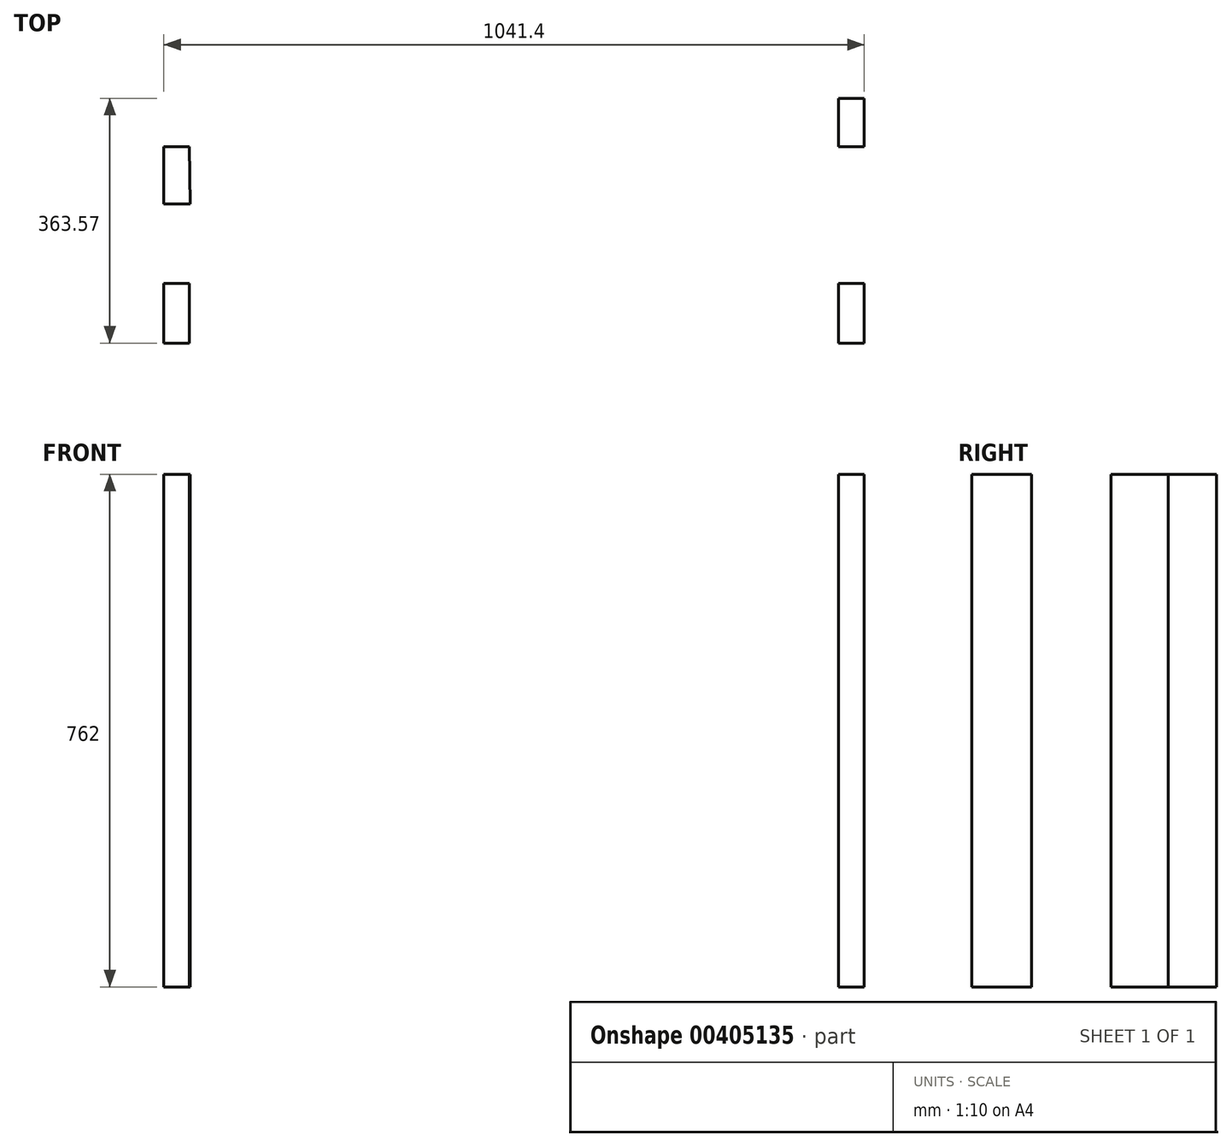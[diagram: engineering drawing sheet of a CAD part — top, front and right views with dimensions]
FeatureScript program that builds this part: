
annotation { "Feature Type Name" : "Feature", "Feature Type Description" : "" }
export const myFeature = defineFeature(function(context is Context, id is Id, definition is map)
    precondition{}
    {
        {
            var Q0;
            Q0=qCreatedBy(makeId("Top.planeOp"),FACE);
            var sketch = newSketch(context, id + "F0", { "sketchPlane" : qUnion([Q0])});
            skLineSegment(sketch, "E0.bottom", {"start": v(0, 0) * mm, "end": v(38.1, 0) * mm});
            skLineSegment(sketch, "E0.top", {"start": v(0, 0) * mm, "end": v(38.1, 0) * mm});
            skLineSegment(sketch, "E0.left", {"start": v(0, 0) * mm, "end": v(0, 0) * mm});
            skLineSegment(sketch, "E0.right", {"start": v(38.1, 0) * mm, "end": v(38.1, 0) * mm});
            skLineSegment(sketch, "E1.bottom", {"start": v(0, -292.1) * mm, "end": v(38.1, -292.1) * mm});
            skLineSegment(sketch, "E1.top", {"start": v(0, -203.2) * mm, "end": v(38.1, -203.2) * mm});
            skLineSegment(sketch, "E1.left", {"start": v(0, -292.1) * mm, "end": v(0, -203.2) * mm});
            skLineSegment(sketch, "E1.right", {"start": v(38.1, -292.1) * mm, "end": v(38.1, -203.2) * mm});
            skLineSegment(sketch, "E2.bottom", {"start": v(1041.4, 0) * mm, "end": v(1003.3, 0) * mm});
            skLineSegment(sketch, "E2.top", {"start": v(1041.4, 0) * mm, "end": v(1003.3, 0) * mm});
            skLineSegment(sketch, "E2.left", {"start": v(1003.3, 0) * mm, "end": v(1003.3, 0) * mm});
            skLineSegment(sketch, "E2.right", {"start": v(1041.4, 0) * mm, "end": v(1041.4, 0) * mm});
            skLineSegment(sketch, "E3.bottom", {"start": v(1003.3, -203.2) * mm, "end": v(1041.4, -203.2) * mm});
            skLineSegment(sketch, "E3.top", {"start": v(1003.3, -292.1) * mm, "end": v(1041.4, -292.1) * mm});
            skLineSegment(sketch, "E3.left", {"start": v(1003.3, -203.2) * mm, "end": v(1003.3, -292.1) * mm});
            skLineSegment(sketch, "E3.right", {"start": v(1041.4, -203.2) * mm, "end": v(1041.4, -292.1) * mm});
            skLineSegment(sketch, "E4", {"start": v(0, 0) * mm, "end": v(0, -85.3) * mm});
            skLineSegment(sketch, "E5", {"start": v(0, -85.3) * mm, "end": v(39.14, -85.3) * mm});
            skLineSegment(sketch, "E6", {"start": v(39.14, -85.3) * mm, "end": v(39.14, -85.3) * mm});
            skLineSegment(sketch, "E7", {"start": v(39.14, -85.3) * mm, "end": v(38.1, 0) * mm});
            skLineSegment(sketch, "E8", {"start": v(1041.4, 0) * mm, "end": v(1041.4, 71.47) * mm});
            skLineSegment(sketch, "E9", {"start": v(1041.4, 71.47) * mm, "end": v(1003.3, 71.47) * mm});
            skLineSegment(sketch, "E10", {"start": v(1003.3, 71.47) * mm, "end": v(1003.3, 71.47) * mm});
            skLineSegment(sketch, "E11", {"start": v(1003.3, 71.47) * mm, "end": v(1003.3, 0) * mm});
            skSolve(sketch);
        }
        {
            var Q0;
            Q0 = qSketchRegion(id + "F0", true);
            extrude(context, id + "F1", {"entities" : qUnion([Q0]), "depth" : 762 * mm});
        }
    });
